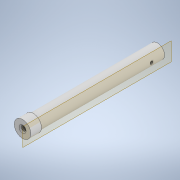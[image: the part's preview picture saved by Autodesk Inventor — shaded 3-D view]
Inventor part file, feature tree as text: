
AUTODESK INVENTOR PART (.ipt)
format: ipt  version: 2021.3 (Build 253353000, 353)  size: 131,072 bytes
history: native  units: mm
features: sketch x4, hole x3, revolve x1, chamfer x1, plane x1
ambient origin geometry x8: Origin, YZ Plane, XZ Plane, XY Plane, X Axis, Y Axis, Z Axis, Center Point
bodies: Body1 (feature_tree)
feature tree (10):
  revolve  "Umdrehung2"
  hole  "Bohrung2"  [1 undecoded]
  hole  "Bohrung3"  [1 undecoded]
  chamfer  "Fase2"  Distance=2.0mm Angle=45.0deg
  plane  "Arbeitsebene2"
  hole  "Bohrung4"  [1 undecoded]
  sketch  "Skizze1"  dims[d0=7.0mm d1=6.0mm]
  sketch  "Skizze3"  dims[d2=9.0mm d3=105.0mm]
  sketch  "Skizze4"  dims[d20=90.0deg]
  sketch  "Skizze5"  dims[d21=6.647mm d22=7.5mm d23=4.0mm d24=2.0mm d25=90.0deg d26=8.0mm d27=20.594885mm d28=4.0mm d29=7.5mm d30=4.0mm d31=2.0mm d32=90.0deg d33=8.0mm d34=20.594885mm d35=1.0mm d36=2.0mm d37=45.0deg d38=6.0mm d39=11.0mm d40=2.459mm d41=6.0mm d42=4.0mm d43=2.0mm d44=90.0deg d45=8.0mm d46=20.594885mm]
note: 3 required parameter values undecoded (feature->parameter linkage not recoverable at this tier; creation-order binding heuristic only, values carry confidence <= 0.55)
